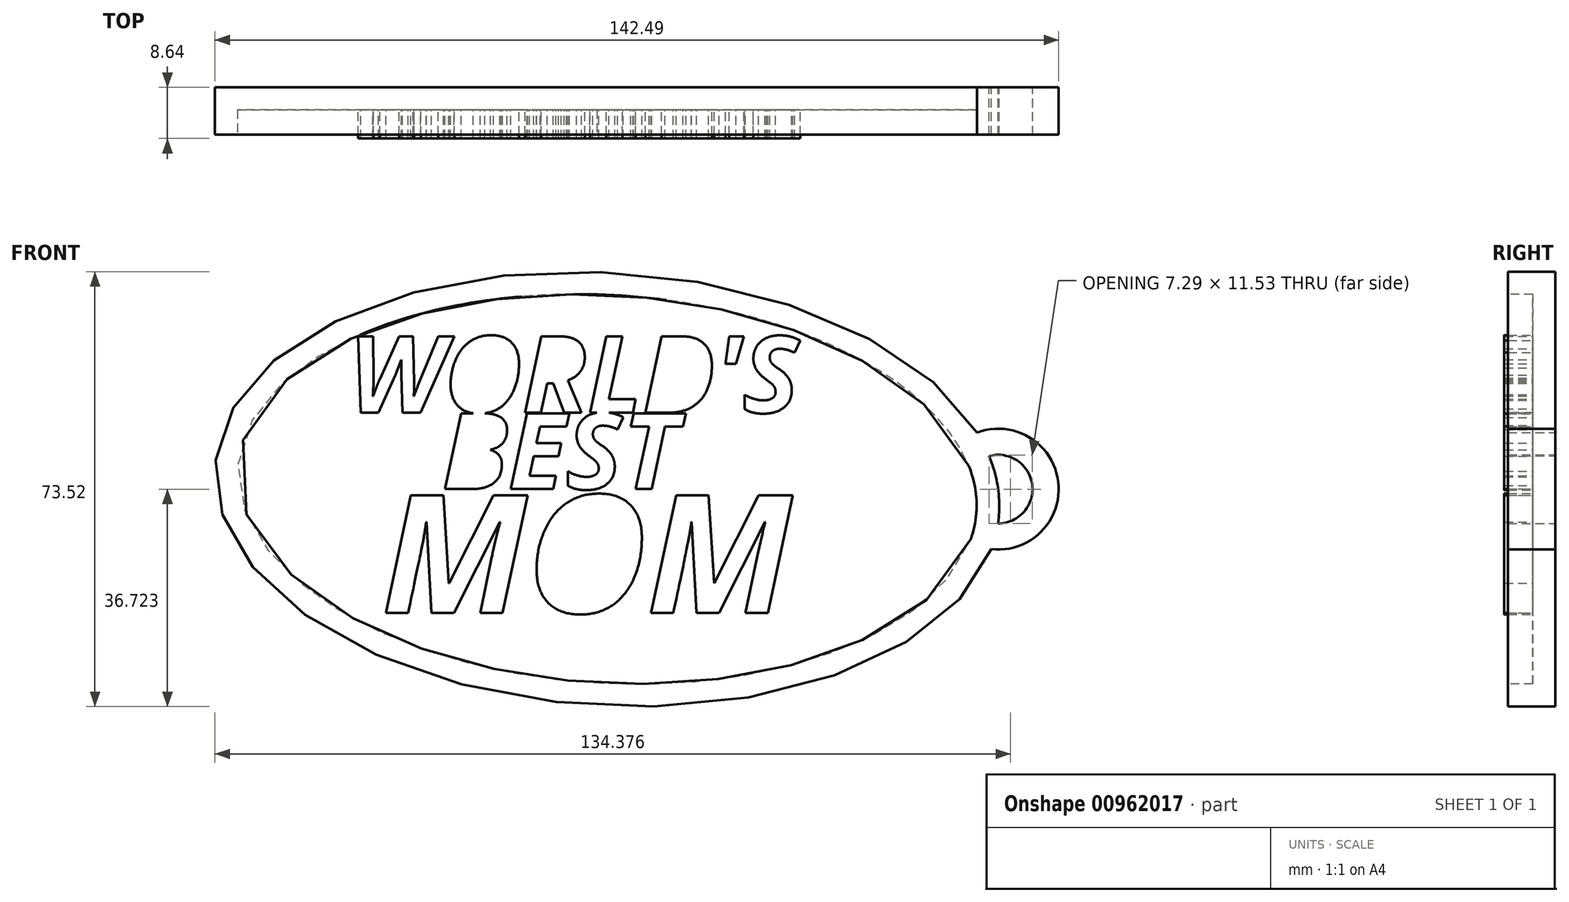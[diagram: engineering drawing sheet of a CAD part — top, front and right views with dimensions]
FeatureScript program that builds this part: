
annotation { "Feature Type Name" : "Feature", "Feature Type Description" : "" }
export const myFeature = defineFeature(function(context is Context, id is Id, definition is map)
    precondition{}
    {
        {
            var Q0;
            Q0=qCreatedBy(makeId("Front.planeOp"),FACE);
            var sketch = newSketch(context, id + "F0", { "sketchPlane" : qUnion([Q0])});
            skEllipse(sketch, "E0", {"center": v(0, 0) * mm, "majorRadius": 66.31 * mm, "minorRadius": 36.61 * mm, "majorAxis": v(1, -0.06)});
            skArc(sketch, "E1", {"start": v(64.86, -10.15) * mm, "mid": v(76.18, 1.24) * mm, "end": v(62.45, 9.57) * mm});
            skArc(sketch, "E2", {"start": v(66, -5.8) * mm, "mid": v(71.8, 0.76) * mm, "end": v(64.5, 5.6) * mm});
            skSolve(sketch);
        }
        {
            var Q0;
            Q0=qSketchRegion(id+"F0",true);
            extrude(context, id + "F1", {"entities" : qUnion([Q0]), "depth" : 8 * mm, "offsetDistance" : 25.4 * mm});
        }
        {
            var Q0;
            Q0=makeQuery(id+"F1.opExtrude","CAP_FACE",FACE,{"disambiguationData":[OSD([sQuery(id+"F0.wireOp",EDGE,"E0"),sQuery(id+"F0.wireOp",EDGE,"E1"),sQuery(id+"F0.wireOp",EDGE,"E2")])],"isStart":false});
            shell(context, id + "F2", {"entities" : qUnion([Q0]), "thickness" : 3.8 * mm});
        }
        {
            var Q0;
            Q0=qCreatedBy(makeId("Front.planeOp"),FACE);
            var sketch = newSketch(context, id + "F3", { "sketchPlane" : qUnion([Q0])});
            skText(sketch, "E3", { "text": "WORLD\'S", "fontName": "OpenSans-BoldItalic.ttf"});
            skText(sketch, "E4", { "text": "BEST", "fontName": "OpenSans-BoldItalic.ttf"});
            skText(sketch, "E5", { "text": "MOM", "fontName": "OpenSans-BoldItalic.ttf"});
            const initialGuessF3  = {"E3": [-0.04365, 0.01292, 1, 0, 0.013], "E4": [-0.02785, 0, 1, 0, 0.01292], "E5": [-0.03806, -0.02093, 1, 0, 0.02003]};
            skSetInitialGuess(sketch, initialGuessF3);
            skSolve(sketch);
        }
        {
            var Q0;
            Q0=makeQuery(id+"F3.imprint","IMPRINT",FACE,{"disambiguationData":[TD([[makeQuery(id+"F3.imprint","IMPRINT",EDGE,{"derivedFrom":sQuery(id+"F3.wireOp",EDGE,"E3.sketch_text.stroke-0")}),-1.0]])]});
            var Q1;
            Q1=makeQuery(id+"F3.imprint","IMPRINT",FACE,{"disambiguationData":[TD([[makeQuery(id+"F3.imprint","IMPRINT",EDGE,{"derivedFrom":sQuery(id+"F3.wireOp",EDGE,"E3.sketch_text.stroke-86")}),-1.0]])]});
            var Q2;
            Q2=makeQuery(id+"F3.imprint","IMPRINT",FACE,{"disambiguationData":[TD([[makeQuery(id+"F3.imprint","IMPRINT",EDGE,{"derivedFrom":sQuery(id+"F3.wireOp",EDGE,"E3.sketch_text.stroke-90")}),-1.0]])]});
            var Q3;
            Q3=makeQuery(id+"F3.imprint","IMPRINT",FACE,{"disambiguationData":[TD([[makeQuery(id+"F3.imprint","IMPRINT",EDGE,{"derivedFrom":sQuery(id+"F3.wireOp",EDGE,"E4.sketch_text.stroke-24")}),-1.0]])]});
            var Q4;
            Q4=makeQuery(id+"F3.imprint","IMPRINT",FACE,{"disambiguationData":[TD([[makeQuery(id+"F3.imprint","IMPRINT",EDGE,{"derivedFrom":sQuery(id+"F3.wireOp",EDGE,"E4.sketch_text.stroke-60")}),-1.0]])]});
            var Q5;
            Q5=makeQuery(id+"F3.imprint","IMPRINT",FACE,{"disambiguationData":[TD([[makeQuery(id+"F3.imprint","IMPRINT",EDGE,{"derivedFrom":sQuery(id+"F3.wireOp",EDGE,"E5.sketch_text.stroke-0")}),-1.0]])]});
            var Q6;
            Q6=makeQuery(id+"F3.imprint","IMPRINT",FACE,{"disambiguationData":[TD([[makeQuery(id+"F3.imprint","IMPRINT",EDGE,{"derivedFrom":sQuery(id+"F3.wireOp",EDGE,"E5.sketch_text.stroke-38")}),-1.0]])]});
            var Q7;
            Q7=makeQuery(id+"F3.imprint","IMPRINT",FACE,{"disambiguationData":[TD([[makeQuery(id+"F3.imprint","IMPRINT",EDGE,{"derivedFrom":sQuery(id+"F3.wireOp",EDGE,"E3.sketch_text.stroke-45")}),-1.0]])]});
            var Q8;
            {var subQ0=sQuery(id+"F3.wireOp",EDGE,"E3.sketch_text.stroke-64");Q8=makeQuery(id+"F3.imprint","IMPRINT",FACE,{"disambiguationData":[TD([[makeQuery(id+"F3.imprint","IMPRINT",EDGE,{"derivedFrom":subQ0}),-1.0]])]});}
            var Q9;
            Q9=makeQuery(id+"F3.imprint","IMPRINT",FACE,{"disambiguationData":[TD([[makeQuery(id+"F3.imprint","IMPRINT",EDGE,{"derivedFrom":sQuery(id+"F3.wireOp",EDGE,"E3.sketch_text.stroke-70")}),-1.0]])]});
            var Q10;
            Q10=makeQuery(id+"F3.imprint","IMPRINT",FACE,{"disambiguationData":[TD([[makeQuery(id+"F3.imprint","IMPRINT",EDGE,{"derivedFrom":sQuery(id+"F3.wireOp",EDGE,"E3.sketch_text.stroke-25")}),-1.0]])]});
            var Q11;
            {var subQ0=sQuery(id+"F3.wireOp",EDGE,"E3.sketch_text.stroke-28");var subQ1=sQuery(id+"F3.wireOp",EDGE,"E3.sketch_text.stroke-27");var subQ2=makeQuery(id+"F3.imprint","INTERSECT",VERTEX,{"derivedFrom":[subQ1,subQ0]});Q11=makeQuery(id+"F3.imprint","IMPRINT",FACE,{"disambiguationData":[TD([[makeQuery(id+"F3.imprint","IMPRINT",EDGE,{"disambiguationData":[TD([[subQ2,1.0]])],"derivedFrom":subQ1}),-1.0]])]});}
            var Q12;
            {var subQ15=sQuery(id+"F3.wireOp",EDGE,"E4.sketch_text.stroke-36");Q12=makeQuery(id+"F3.imprint","IMPRINT",FACE,{"disambiguationData":[TD([[makeQuery(id+"F3.imprint","IMPRINT",EDGE,{"derivedFrom":subQ15}),-1.0]])]});}
            var Q13;
            {var subQ0=sQuery(id+"F3.wireOp",EDGE,"E4.sketch_text.stroke-51");var subQ1=sQuery(id+"F3.wireOp",EDGE,"E3.sketch_text.stroke-69");var subQ2=makeQuery(id+"F3.imprint","INTERSECT",VERTEX,{"derivedFrom":[subQ1,subQ0]});Q13=makeQuery(id+"F3.imprint","IMPRINT",FACE,{"disambiguationData":[TD([[makeQuery(id+"F3.imprint","IMPRINT",EDGE,{"disambiguationData":[TD([[subQ2,-1.0]])],"derivedFrom":subQ1}),-1.0]])]});}
            var Q14;
            Q14=makeQuery(id+"F3.imprint","IMPRINT",FACE,{"disambiguationData":[TD([[makeQuery(id+"F3.imprint","IMPRINT",EDGE,{"derivedFrom":sQuery(id+"F3.wireOp",EDGE,"E5.sketch_text.stroke-18")}),-1.0]])]});
            var Q15;
            {var subQ0=sQuery(id+"F3.wireOp",EDGE,"E4.sketch_text.stroke-38");var subQ1=sQuery(id+"F3.wireOp",EDGE,"E4.sketch_text.stroke-37");var subQ2=makeQuery(id+"F3.imprint","INTERSECT",VERTEX,{"derivedFrom":[subQ1,subQ0]});Q15=makeQuery(id+"F3.imprint","IMPRINT",FACE,{"disambiguationData":[TD([[makeQuery(id+"F3.imprint","IMPRINT",EDGE,{"disambiguationData":[TD([[subQ2,1.0]])],"derivedFrom":subQ1}),-1.0]])]});}
            var Q16;
            {var subQ4=sQuery(id+"F3.wireOp",EDGE,"E4.sketch_text.stroke-1");Q16=makeQuery(id+"F3.imprint","IMPRINT",FACE,{"disambiguationData":[TD([[makeQuery(id+"F3.imprint","IMPRINT",EDGE,{"derivedFrom":subQ4}),-1.0]])]});}
            var Q17;
            Q17=makeQuery(id+"F3.imprint","IMPRINT",FACE,{"disambiguationData":[TD([[makeQuery(id+"F3.imprint","IMPRINT",EDGE,{"derivedFrom":sQuery(id+"F3.wireOp",EDGE,"E3.sketch_text.stroke-45")}),1.0]])]});
            var Q18;
            Q18=makeQuery(id+"F3.imprint","IMPRINT",FACE,{"disambiguationData":[TD([[makeQuery(id+"F3.imprint","IMPRINT",EDGE,{"derivedFrom":sQuery(id+"F3.wireOp",EDGE,"E5.sketch_text.stroke-28")}),1.0]])]});
            var Q19;
            Q19=makeQuery(id+"F3.imprint","IMPRINT",FACE,{"disambiguationData":[TD([[makeQuery(id+"F3.imprint","IMPRINT",EDGE,{"derivedFrom":sQuery(id+"F3.wireOp",EDGE,"E3.sketch_text.stroke-78")}),1.0]])]});
            var Q20;
            Q20=makeQuery(id+"F3.imprint","IMPRINT",FACE,{"disambiguationData":[TD([[makeQuery(id+"F3.imprint","IMPRINT",EDGE,{"derivedFrom":sQuery(id+"F3.wireOp",EDGE,"E3.sketch_text.stroke-35")}),1.0]])]});
            var Q21;
            Q21=makeQuery(id+"F3.imprint","IMPRINT",FACE,{"disambiguationData":[TD([[makeQuery(id+"F3.imprint","IMPRINT",EDGE,{"derivedFrom":sQuery(id+"F3.wireOp",EDGE,"E4.sketch_text.stroke-18")}),1.0]])]});
            var Q22;
            Q22=makeQuery(id+"F3.imprint","IMPRINT",FACE,{"disambiguationData":[TD([[makeQuery(id+"F3.imprint","IMPRINT",EDGE,{"derivedFrom":sQuery(id+"F3.wireOp",EDGE,"E4.sketch_text.stroke-12")}),1.0]])]});
            extrude(context, id + "F4", {"entities" : qUnion([Q0, Q1, Q2, Q3, Q4, Q5, Q6, Q7, Q8, Q9, Q10, Q11, Q12, Q13, Q14, Q15, Q16, Q17, Q18, Q19, Q20, Q21, Q22]), "operationType" : NewBodyOperationType.ADD, "depth" : 8.64 * mm, "offsetDistance" : 25.4 * mm});
        }
    });
